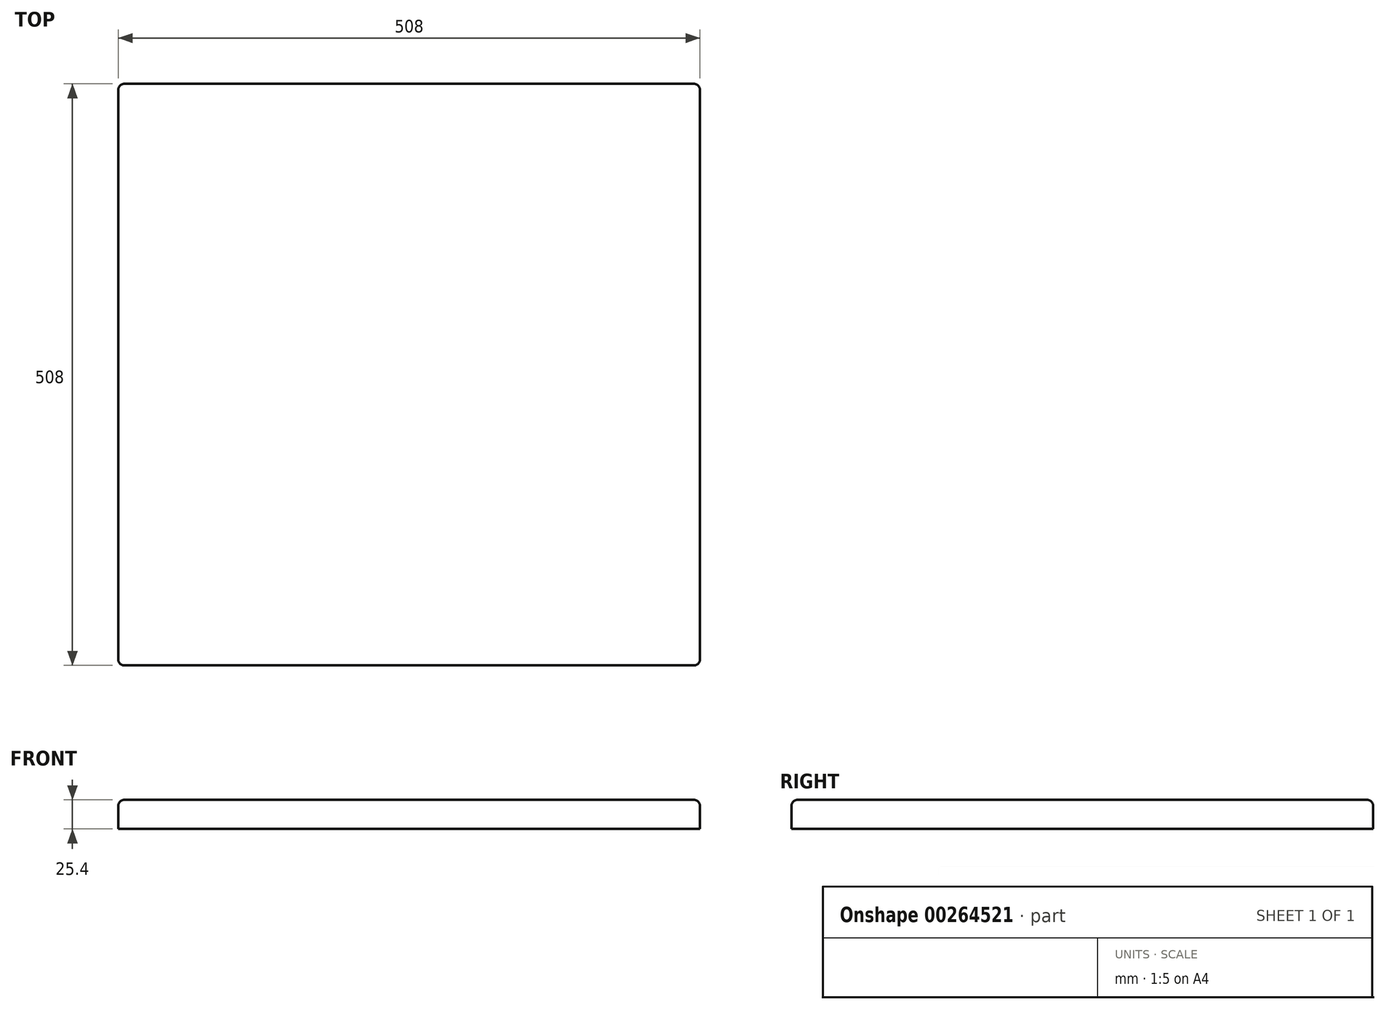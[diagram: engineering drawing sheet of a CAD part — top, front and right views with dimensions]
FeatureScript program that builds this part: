
annotation { "Feature Type Name" : "Feature", "Feature Type Description" : "" }
export const myFeature = defineFeature(function(context is Context, id is Id, definition is map)
    precondition{}
    {
        {
            var Q0;
            Q0=qCreatedBy(makeId("Top.planeOp"),FACE);
            var sketch = newSketch(context, id + "F0", { "sketchPlane" : qUnion([Q0])});
            skLineSegment(sketch, "E0.bottom", {"start": v(-254, 254) * mm, "end": v(254, 254) * mm});
            skLineSegment(sketch, "E0.top", {"start": v(-254, -254) * mm, "end": v(254, -254) * mm});
            skLineSegment(sketch, "E0.left", {"start": v(-254, 254) * mm, "end": v(-254, -254) * mm});
            skLineSegment(sketch, "E0.right", {"start": v(254, 254) * mm, "end": v(254, -254) * mm});
            skPoint(sketch, "E0.middle", {"position": v(0, 0) * mm});
            skSolve(sketch);
        }
        {
            var Q0;
            Q0 = qSketchRegion(id + "F0", true);
            extrude(context, id + "F1", {"entities" : qUnion([Q0]), "depth" : 25.4 * mm, "offsetDistance" : 25.4 * mm, "symmetric" : true});
        }
        {
            var Q0;
            Q0=makeQuery(id+"F1.opExtrude","SWEPT_EDGE",EDGE,{"disambiguationData":[OSD([sQuery(id+"F0.wireOp",EDGE,"E0.top"),sQuery(id+"F0.wireOp",EDGE,"E0.left")])]});
            var Q1;
            Q1=makeQuery(id+"F1.opExtrude","SWEPT_EDGE",EDGE,{"disambiguationData":[OSD([sQuery(id+"F0.wireOp",EDGE,"E0.top"),sQuery(id+"F0.wireOp",EDGE,"E0.right")])]});
            var Q2;
            Q2=makeQuery(id+"F1.opExtrude","SWEPT_EDGE",EDGE,{"disambiguationData":[OSD([sQuery(id+"F0.wireOp",EDGE,"E0.bottom"),sQuery(id+"F0.wireOp",EDGE,"E0.right")])]});
            var Q3;
            Q3=makeQuery(id+"F1.opExtrude","SWEPT_EDGE",EDGE,{"disambiguationData":[OSD([sQuery(id+"F0.wireOp",EDGE,"E0.bottom"),sQuery(id+"F0.wireOp",EDGE,"E0.left")])]});
            fillet(context, id + "F2", {"entities" : qUnion([Q0, Q1, Q2, Q3]), "radius" : 5.08 * mm, "tangentPropagation" : true, "allowEdgeOverflow" : false});
        }
        {
            var Q0;
            Q0=makeQuery(id+"F1.opExtrude","CAP_FACE",FACE,{"disambiguationData":[OSD([sQuery(id+"F0.wireOp",EDGE,"E0.bottom"),sQuery(id+"F0.wireOp",EDGE,"E0.top"),sQuery(id+"F0.wireOp",EDGE,"E0.left"),sQuery(id+"F0.wireOp",EDGE,"E0.right")])],"isStart":false});
            fillet(context, id + "F3", {"entities" : qUnion([Q0]), "radius" : 5.08 * mm, "tangentPropagation" : true, "allowEdgeOverflow" : false});
        }
    });
